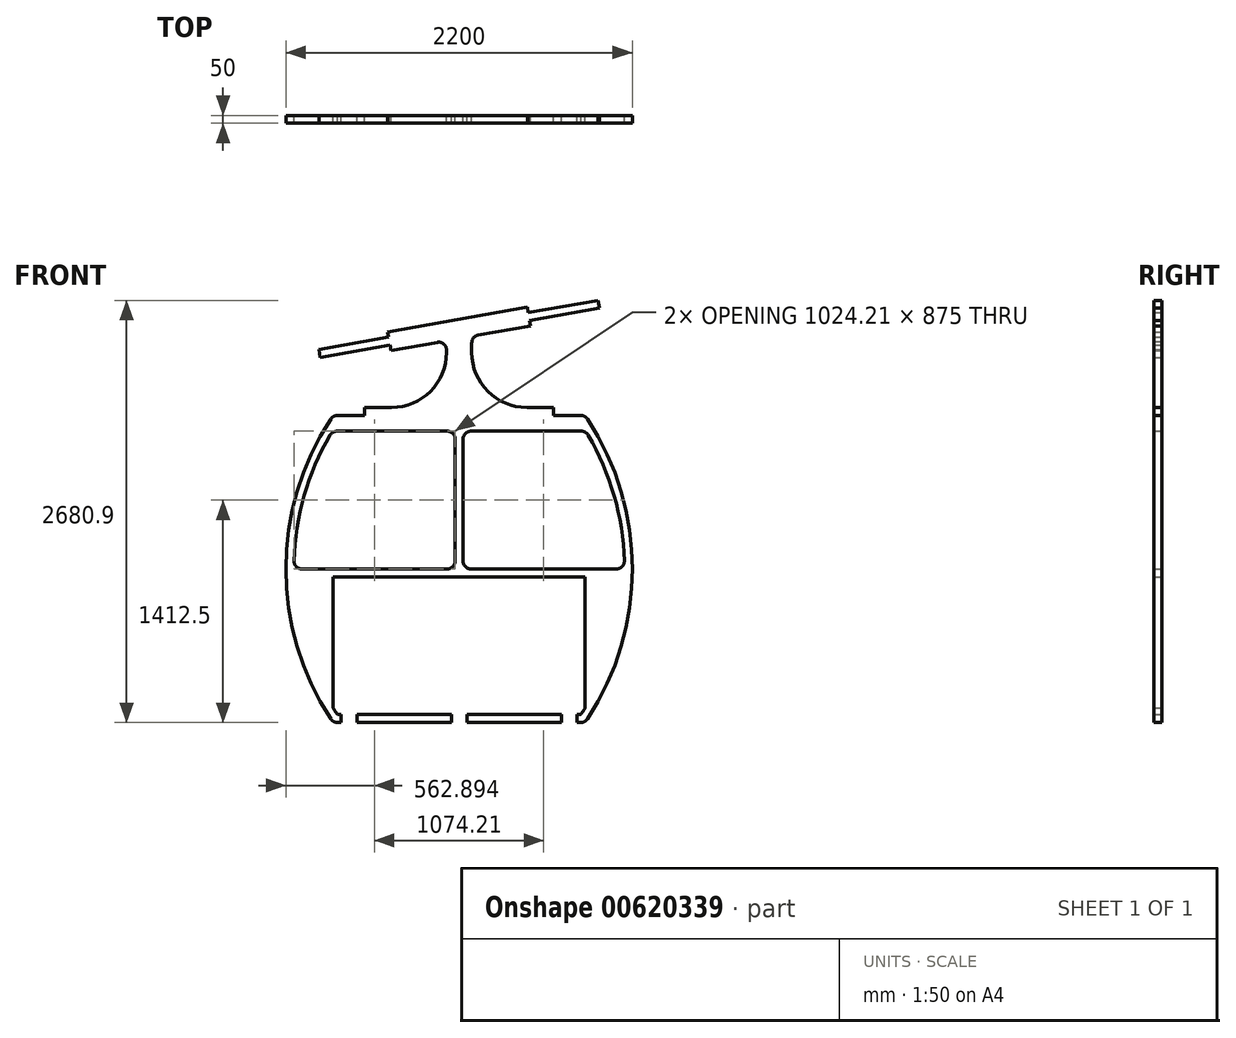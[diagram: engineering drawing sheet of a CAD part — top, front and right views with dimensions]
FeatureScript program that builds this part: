
annotation { "Feature Type Name" : "Feature", "Feature Type Description" : "" }
export const myFeature = defineFeature(function(context is Context, id is Id, definition is map)
    precondition{}
    {
        {
            var Q0;
            Q0=qCreatedBy(makeId("Front.planeOp"),FACE);
            var sketch = newSketch(context, id + "F0", { "sketchPlane" : qUnion([Q0])});
            skLineSegment(sketch, "E0.bottom", {"start": v(-1600, 1950) * mm, "end": v(0, 1950) * mm});
            skLineSegment(sketch, "E0.top", {"start": v(-1600, 0) * mm, "end": v(0, 0) * mm});
            skLineSegment(sketch, "E0.left", {"start": v(-1600, 1950) * mm, "end": v(-1600, 0) * mm});
            skLineSegment(sketch, "E0.right", {"start": v(0, 1950) * mm, "end": v(0, 0) * mm});
            skArc(sketch, "E1", {"start": v(0, 0) * mm, "mid": v(300, 975) * mm, "end": v(0, 1950) * mm});
            skArc(sketch, "E2", {"start": v(-1600, 1950) * mm, "mid": v(-1900, 975) * mm, "end": v(-1600, 0) * mm});
            skArc(sketch, "E3", {"start": v(-1604.9, 1850) * mm, "mid": v(-1849.74, 945.42) * mm, "end": v(-1573.28, 50) * mm});
            skArc(sketch, "E4", {"start": v(-26.72, 50) * mm, "mid": v(249.74, 945.42) * mm, "end": v(4.9, 1850) * mm});
            skLineSegment(sketch, "E5", {"start": v(-1850, 975) * mm, "end": v(250, 975) * mm});
            skPoint(sketch, "E5.startSnap0", {"position": v(-1900, 975) * mm});
            skLineSegment(sketch, "E6", {"start": v(-1604.9, 1850) * mm, "end": v(4.9, 1850) * mm});
            skLineSegment(sketch, "E7", {"start": v(-1573.28, 50) * mm, "end": v(-26.72, 50) * mm});
            skLineSegment(sketch, "E8", {"start": v(-800, 1950) * mm, "end": v(-800, 975) * mm});
            skLineSegment(sketch, "E9", {"start": v(-1400, 1950) * mm, "end": v(-1400, 2000) * mm});
            skLineSegment(sketch, "E10", {"start": v(-200, 1950) * mm, "end": v(-200, 2000) * mm});
            skLineSegment(sketch, "E11", {"start": v(-880, 2500) * mm, "end": v(-880, 2350) * mm});
            skLineSegment(sketch, "E12", {"start": v(-720, 2500) * mm, "end": v(-720, 2350) * mm});
            skLineSegment(sketch, "E13", {"start": v(-880, 2500) * mm, "end": v(-720, 2500) * mm});
            skLineSegment(sketch, "E14", {"start": v(-825, 1850) * mm, "end": v(-825, 975) * mm});
            skLineSegment(sketch, "E15", {"start": v(-825, 975) * mm, "end": v(-775, 975) * mm});
            skLineSegment(sketch, "E16", {"start": v(-775, 975) * mm, "end": v(-775, 1850) * mm});
            skLineSegment(sketch, "E17", {"start": v(-1400, 2000) * mm, "end": v(-1230, 2000) * mm});
            skLineSegment(sketch, "E18", {"start": v(-200, 2000) * mm, "end": v(-370, 2000) * mm});
            skArc(sketch, "E19", {"start": v(-1230, 2000) * mm, "mid": v(-982.51, 2102.51) * mm, "end": v(-880, 2350) * mm});
            skArc(sketch, "E20", {"start": v(-720, 2350) * mm, "mid": v(-617.49, 2102.51) * mm, "end": v(-370, 2000) * mm});
            skLineSegment(sketch, "E21", {"start": v(-1243.16, 2421.86) * mm, "end": v(-356.84, 2578.14) * mm});
            skCircle(sketch, "E22", {"center": v(-1243.16, 2421.86) * mm, "radius": 60 * mm});
            skCircle(sketch, "E23", {"center": v(-356.84, 2578.14) * mm, "radius": 60 * mm});
            skLineSegment(sketch, "E24", {"start": v(-810.42, 2559.09) * mm, "end": v(-800, 2500) * mm});
            skPoint(sketch, "E25.end.orphan", {"position": v(-1450.54, 2446.22) * mm});
            skPoint(sketch, "E26.start.orphan", {"position": v(-170.3, 2671.96) * mm});
            skLineSegment(sketch, "E27", {"start": v(-367.26, 2637.23) * mm, "end": v(-1253.58, 2480.95) * mm});
            skLineSegment(sketch, "E28", {"start": v(-1232.74, 2362.77) * mm, "end": v(-346.42, 2519.05) * mm});
            skLineSegment(sketch, "E29", {"start": v(81.99, 2680.9) * mm, "end": v(-1690.67, 2368.34) * mm});
            skLineSegment(sketch, "E30", {"start": v(-1690.67, 2368.34) * mm, "end": v(-1681.99, 2319.1) * mm});
            skLineSegment(sketch, "E31", {"start": v(-1681.99, 2319.1) * mm, "end": v(90.67, 2631.66) * mm});
            skLineSegment(sketch, "E32", {"start": v(90.67, 2631.66) * mm, "end": v(81.99, 2680.9) * mm});
            skLineSegment(sketch, "E33", {"start": v(-1253.58, 2480.95) * mm, "end": v(-1232.74, 2362.77) * mm});
            skLineSegment(sketch, "E34", {"start": v(-367.26, 2637.23) * mm, "end": v(-346.42, 2519.05) * mm});
            skLineSegment(sketch, "E35", {"start": v(-1899.28, 925) * mm, "end": v(299.28, 925) * mm});
            skLineSegment(sketch, "E36", {"start": v(-825, 975) * mm, "end": v(-825, 925) * mm});
            skLineSegment(sketch, "E37", {"start": v(-775, 975) * mm, "end": v(-775, 925) * mm});
            skLineSegment(sketch, "E38", {"start": v(-1550, 0) * mm, "end": v(-1550, 50) * mm});
            skLineSegment(sketch, "E39", {"start": v(-1550, 50) * mm, "end": v(-1450, 50) * mm});
            skLineSegment(sketch, "E40", {"start": v(-1450, 50) * mm, "end": v(-1450, 0) * mm});
            skLineSegment(sketch, "E41", {"start": v(-850, 0) * mm, "end": v(-850, 50) * mm});
            skLineSegment(sketch, "E42", {"start": v(-850, 50) * mm, "end": v(-750, 50) * mm});
            skLineSegment(sketch, "E43", {"start": v(-750, 50) * mm, "end": v(-750, 0) * mm});
            skLineSegment(sketch, "E44", {"start": v(-150, 0) * mm, "end": v(-150, 50) * mm});
            skLineSegment(sketch, "E45", {"start": v(-150, 50) * mm, "end": v(-50, 50) * mm});
            skLineSegment(sketch, "E46", {"start": v(-50, 50) * mm, "end": v(-50, 0) * mm});
            skLineSegment(sketch, "E47", {"start": v(-800, 50) * mm, "end": v(-800, 0) * mm});
            skSolve(sketch);
        }
        {
            var Q0;
            {var subQ0=sQuery(id+"F0.wireOp",EDGE,"E40");var subQ1=sQuery(id+"F0.wireOp",EDGE,"E0.top");var subQ2=makeQuery(id+"F0.imprint","INTERSECT",VERTEX,{"derivedFrom":[subQ1,subQ0]});Q0=makeQuery(id+"F0.imprint","IMPRINT",FACE,{"disambiguationData":[TD([[makeQuery(id+"F0.imprint","IMPRINT",EDGE,{"disambiguationData":[TD([[subQ2,-1.0]])],"derivedFrom":subQ1}),1.0]])]});}
            var Q1;
            {var subQ0=sQuery(id+"F0.wireOp",EDGE,"E43");var subQ1=sQuery(id+"F0.wireOp",EDGE,"E0.top");var subQ2=makeQuery(id+"F0.imprint","INTERSECT",VERTEX,{"derivedFrom":[subQ1,subQ0]});Q1=makeQuery(id+"F0.imprint","IMPRINT",FACE,{"disambiguationData":[TD([[makeQuery(id+"F0.imprint","IMPRINT",EDGE,{"disambiguationData":[TD([[subQ2,-1.0]])],"derivedFrom":subQ1}),1.0]])]});}
            var Q2;
            {var subQ11=sQuery(id+"F0.wireOp",EDGE,"E39");Q2=makeQuery(id+"F0.imprint","IMPRINT",FACE,{"disambiguationData":[TD([[makeQuery(id+"F0.imprint","IMPRINT",EDGE,{"derivedFrom":subQ11}),1.0]])]});}
            var Q3;
            {var subQ1=sQuery(id+"F0.wireOp",EDGE,"E0.left");var subQ3=sQuery(id+"F0.wireOp",EDGE,"E3");var subQ4=makeQuery(id+"F0.imprint","INTERSECT",VERTEX,{"derivedFrom":[subQ1,subQ3]});Q3=makeQuery(id+"F0.imprint","IMPRINT",FACE,{"disambiguationData":[TD([[makeQuery(id+"F0.imprint","IMPRINT",EDGE,{"disambiguationData":[TD([[subQ4,1.0]])],"derivedFrom":subQ3}),-1.0]])]});}
            var Q4;
            {var subQ4=sQuery(id+"F0.wireOp",EDGE,"E0.bottom");var subQ6=sQuery(id+"F0.wireOp",EDGE,"E8");var subQ7=makeQuery(id+"F0.imprint","INTERSECT",VERTEX,{"derivedFrom":[subQ4,subQ6]});Q4=makeQuery(id+"F0.imprint","IMPRINT",FACE,{"disambiguationData":[TD([[makeQuery(id+"F0.imprint","IMPRINT",EDGE,{"disambiguationData":[TD([[subQ7,1.0]])],"derivedFrom":subQ4}),-1.0]])]});}
            var Q5;
            {var subQ2=sQuery(id+"F0.wireOp",EDGE,"E8");var subQ4=sQuery(id+"F0.wireOp",EDGE,"E0.bottom");var subQ5=makeQuery(id+"F0.imprint","INTERSECT",VERTEX,{"derivedFrom":[subQ4,subQ2]});Q5=makeQuery(id+"F0.imprint","IMPRINT",FACE,{"disambiguationData":[TD([[makeQuery(id+"F0.imprint","IMPRINT",EDGE,{"disambiguationData":[TD([[subQ5,-1.0]])],"derivedFrom":subQ4}),-1.0]])]});}
            var Q6;
            {var subQ1=sQuery(id+"F0.wireOp",EDGE,"E0.right");var subQ3=sQuery(id+"F0.wireOp",EDGE,"E4");var subQ4=makeQuery(id+"F0.imprint","INTERSECT",VERTEX,{"derivedFrom":[subQ1,subQ3]});Q6=makeQuery(id+"F0.imprint","IMPRINT",FACE,{"disambiguationData":[TD([[makeQuery(id+"F0.imprint","IMPRINT",EDGE,{"disambiguationData":[TD([[subQ4,-1.0]])],"derivedFrom":subQ3}),-1.0]])]});}
            var Q7;
            {var subQ8=sQuery(id+"F0.wireOp",EDGE,"E9");Q7=makeQuery(id+"F0.imprint","IMPRINT",FACE,{"disambiguationData":[TD([[makeQuery(id+"F0.imprint","IMPRINT",EDGE,{"derivedFrom":subQ8}),-1.0]])]});}
            var Q8;
            {var subQ0=sQuery(id+"F0.wireOp",EDGE,"E14");Q8=makeQuery(id+"F0.imprint","IMPRINT",FACE,{"disambiguationData":[TD([[makeQuery(id+"F0.imprint","IMPRINT",EDGE,{"derivedFrom":subQ0}),1.0]])]});}
            var Q9;
            {var subQ0=sQuery(id+"F0.wireOp",EDGE,"E16");Q9=makeQuery(id+"F0.imprint","IMPRINT",FACE,{"disambiguationData":[TD([[makeQuery(id+"F0.imprint","IMPRINT",EDGE,{"derivedFrom":subQ0}),1.0]])]});}
            var Q10;
            {var subQ0=sQuery(id+"F0.wireOp",EDGE,"E21");var subQ1=sQuery(id+"F0.wireOp",EDGE,"E11");var subQ2=makeQuery(id+"F0.imprint","INTERSECT",VERTEX,{"derivedFrom":[subQ1,subQ0]});Q10=makeQuery(id+"F0.imprint","IMPRINT",FACE,{"disambiguationData":[TD([[makeQuery(id+"F0.imprint","IMPRINT",EDGE,{"disambiguationData":[TD([[subQ2,-1.0]])],"derivedFrom":subQ1}),-1.0]])]});}
            var Q11;
            {var subQ0=sQuery(id+"F0.wireOp",EDGE,"E33");var subQ1=sQuery(id+"F0.wireOp",EDGE,"E21");var subQ2=makeQuery(id+"F0.imprint","INTERSECT",VERTEX,{"derivedFrom":[subQ1,subQ0]});Q11=makeQuery(id+"F0.imprint","IMPRINT",FACE,{"disambiguationData":[TD([[makeQuery(id+"F0.imprint","IMPRINT",EDGE,{"disambiguationData":[TD([[subQ2,-1.0]])],"derivedFrom":subQ1}),1.0]])]});}
            var Q12;
            {var subQ1=sQuery(id+"F0.wireOp",EDGE,"E11");var subQ5=sQuery(id+"F0.wireOp",EDGE,"E13");var subQ6=makeQuery(id+"F0.imprint","INTERSECT",VERTEX,{"derivedFrom":[subQ1,subQ5]});Q12=makeQuery(id+"F0.imprint","IMPRINT",FACE,{"disambiguationData":[TD([[makeQuery(id+"F0.imprint","IMPRINT",EDGE,{"disambiguationData":[TD([[subQ6,-1.0]])],"derivedFrom":subQ1}),-1.0]])]});}
            var Q13;
            {var subQ0=sQuery(id+"F0.wireOp",EDGE,"E28");var subQ1=sQuery(id+"F0.wireOp",EDGE,"E11");var subQ2=makeQuery(id+"F0.imprint","INTERSECT",VERTEX,{"derivedFrom":[subQ1,subQ0]});Q13=makeQuery(id+"F0.imprint","IMPRINT",FACE,{"disambiguationData":[TD([[makeQuery(id+"F0.imprint","IMPRINT",EDGE,{"disambiguationData":[TD([[subQ2,1.0]])],"derivedFrom":subQ1}),-1.0]])]});}
            var Q14;
            {var subQ3=sQuery(id+"F0.wireOp",EDGE,"E21");var subQ5=sQuery(id+"F0.wireOp",EDGE,"E11");var subQ6=makeQuery(id+"F0.imprint","INTERSECT",VERTEX,{"derivedFrom":[subQ5,subQ3]});Q14=makeQuery(id+"F0.imprint","IMPRINT",FACE,{"disambiguationData":[TD([[makeQuery(id+"F0.imprint","IMPRINT",EDGE,{"disambiguationData":[TD([[subQ6,-1.0]])],"derivedFrom":subQ5}),1.0]])]});}
            var Q15;
            {var subQ0=sQuery(id+"F0.wireOp",EDGE,"E34");var subQ1=sQuery(id+"F0.wireOp",EDGE,"E21");var subQ2=makeQuery(id+"F0.imprint","INTERSECT",VERTEX,{"derivedFrom":[subQ1,subQ0]});Q15=makeQuery(id+"F0.imprint","IMPRINT",FACE,{"disambiguationData":[TD([[makeQuery(id+"F0.imprint","IMPRINT",EDGE,{"disambiguationData":[TD([[subQ2,1.0]])],"derivedFrom":subQ1}),1.0]])]});}
            var Q16;
            {var subQ5=sQuery(id+"F0.wireOp",EDGE,"E13");var subQ7=sQuery(id+"F0.wireOp",EDGE,"E12");var subQ8=makeQuery(id+"F0.imprint","INTERSECT",VERTEX,{"derivedFrom":[subQ7,subQ5]});Q16=makeQuery(id+"F0.imprint","IMPRINT",FACE,{"disambiguationData":[TD([[makeQuery(id+"F0.imprint","IMPRINT",EDGE,{"disambiguationData":[TD([[subQ8,-1.0]])],"derivedFrom":subQ7}),1.0]])]});}
            var Q17;
            {var subQ0=sQuery(id+"F0.wireOp",EDGE,"E13");var subQ1=sQuery(id+"F0.wireOp",EDGE,"E11");var subQ2=makeQuery(id+"F0.imprint","INTERSECT",VERTEX,{"derivedFrom":[subQ1,subQ0]});Q17=makeQuery(id+"F0.imprint","IMPRINT",FACE,{"disambiguationData":[TD([[makeQuery(id+"F0.imprint","IMPRINT",EDGE,{"disambiguationData":[TD([[subQ2,-1.0]])],"derivedFrom":subQ1}),1.0]])]});}
            var Q18;
            {var subQ0=sQuery(id+"F0.wireOp",EDGE,"E27");var subQ5=sQuery(id+"F0.wireOp",EDGE,"E24");var subQ6=makeQuery(id+"F0.imprint","INTERSECT",VERTEX,{"derivedFrom":[subQ5,subQ0]});Q18=makeQuery(id+"F0.imprint","IMPRINT",FACE,{"disambiguationData":[TD([[makeQuery(id+"F0.imprint","IMPRINT",EDGE,{"disambiguationData":[TD([[subQ6,-1.0]])],"derivedFrom":subQ5}),1.0]])]});}
            var Q19;
            {var subQ1=sQuery(id+"F0.wireOp",EDGE,"E21");var subQ3=sQuery(id+"F0.wireOp",EDGE,"E23");var subQ4=makeQuery(id+"F0.imprint","INTERSECT",VERTEX,{"derivedFrom":[subQ1,subQ3]});Q19=makeQuery(id+"F0.imprint","IMPRINT",FACE,{"disambiguationData":[TD([[makeQuery(id+"F0.imprint","IMPRINT",EDGE,{"disambiguationData":[TD([[subQ4,1.0]])],"derivedFrom":subQ3}),-1.0]])]});}
            var Q20;
            {var subQ0=sQuery(id+"F0.wireOp",EDGE,"E27");var subQ5=sQuery(id+"F0.wireOp",EDGE,"E24");var subQ6=makeQuery(id+"F0.imprint","INTERSECT",VERTEX,{"derivedFrom":[subQ5,subQ0]});Q20=makeQuery(id+"F0.imprint","IMPRINT",FACE,{"disambiguationData":[TD([[makeQuery(id+"F0.imprint","IMPRINT",EDGE,{"disambiguationData":[TD([[subQ6,-1.0]])],"derivedFrom":subQ5}),-1.0]])]});}
            var Q21;
            {var subQ0=sQuery(id+"F0.wireOp",EDGE,"E28");var subQ1=sQuery(id+"F0.wireOp",EDGE,"E12");var subQ2=makeQuery(id+"F0.imprint","INTERSECT",VERTEX,{"derivedFrom":[subQ1,subQ0]});Q21=makeQuery(id+"F0.imprint","IMPRINT",FACE,{"disambiguationData":[TD([[makeQuery(id+"F0.imprint","IMPRINT",EDGE,{"disambiguationData":[TD([[subQ2,1.0]])],"derivedFrom":subQ1}),1.0]])]});}
            var Q22;
            {var subQ0=sQuery(id+"F0.wireOp",EDGE,"E28");var subQ1=sQuery(id+"F0.wireOp",EDGE,"E11");var subQ2=makeQuery(id+"F0.imprint","INTERSECT",VERTEX,{"derivedFrom":[subQ1,subQ0]});Q22=makeQuery(id+"F0.imprint","IMPRINT",FACE,{"disambiguationData":[TD([[makeQuery(id+"F0.imprint","IMPRINT",EDGE,{"disambiguationData":[TD([[subQ2,1.0]])],"derivedFrom":subQ1}),1.0]])]});}
            var Q23;
            {var subQ0=sQuery(id+"F0.wireOp",EDGE,"E33");var subQ1=sQuery(id+"F0.wireOp",EDGE,"E21");var subQ2=makeQuery(id+"F0.imprint","INTERSECT",VERTEX,{"derivedFrom":[subQ1,subQ0]});Q23=makeQuery(id+"F0.imprint","IMPRINT",FACE,{"disambiguationData":[TD([[makeQuery(id+"F0.imprint","IMPRINT",EDGE,{"disambiguationData":[TD([[subQ2,-1.0]])],"derivedFrom":subQ1}),-1.0]])]});}
            var Q24;
            {var subQ0=sQuery(id+"F0.wireOp",EDGE,"E34");var subQ1=sQuery(id+"F0.wireOp",EDGE,"E21");var subQ2=makeQuery(id+"F0.imprint","INTERSECT",VERTEX,{"derivedFrom":[subQ1,subQ0]});Q24=makeQuery(id+"F0.imprint","IMPRINT",FACE,{"disambiguationData":[TD([[makeQuery(id+"F0.imprint","IMPRINT",EDGE,{"disambiguationData":[TD([[subQ2,1.0]])],"derivedFrom":subQ1}),-1.0]])]});}
            var Q25;
            {var subQ5=sQuery(id+"F0.wireOp",EDGE,"E30");Q25=makeQuery(id+"F0.imprint","IMPRINT",FACE,{"disambiguationData":[TD([[makeQuery(id+"F0.imprint","IMPRINT",EDGE,{"derivedFrom":subQ5}),1.0]])]});}
            var Q26;
            {var subQ1=sQuery(id+"F0.wireOp",EDGE,"E22");var subQ3=sQuery(id+"F0.wireOp",EDGE,"E29");var subQ4=makeQuery(id+"F0.imprint","INTERSECT",VERTEX,{"disambiguationData":[OD(1.0)],"derivedFrom":[subQ1,subQ3]});Q26=makeQuery(id+"F0.imprint","IMPRINT",FACE,{"disambiguationData":[TD([[makeQuery(id+"F0.imprint","IMPRINT",EDGE,{"disambiguationData":[TD([[subQ4,-1.0]])],"derivedFrom":subQ3}),-1.0]])]});}
            var Q27;
            {var subQ1=sQuery(id+"F0.wireOp",EDGE,"E23");var subQ3=sQuery(id+"F0.wireOp",EDGE,"E31");var subQ4=makeQuery(id+"F0.imprint","INTERSECT",VERTEX,{"disambiguationData":[OD(1.0)],"derivedFrom":[subQ1,subQ3]});Q27=makeQuery(id+"F0.imprint","IMPRINT",FACE,{"disambiguationData":[TD([[makeQuery(id+"F0.imprint","IMPRINT",EDGE,{"disambiguationData":[TD([[subQ4,-1.0]])],"derivedFrom":subQ3}),-1.0]])]});}
            var Q28;
            {var subQ5=sQuery(id+"F0.wireOp",EDGE,"E32");Q28=makeQuery(id+"F0.imprint","IMPRINT",FACE,{"disambiguationData":[TD([[makeQuery(id+"F0.imprint","IMPRINT",EDGE,{"derivedFrom":subQ5}),1.0]])]});}
            var Q29;
            {var subQ2=sQuery(id+"F0.wireOp",EDGE,"E29");var subQ5=sQuery(id+"F0.wireOp",EDGE,"E22");var subQ8=makeQuery(id+"F0.imprint","INTERSECT",VERTEX,{"disambiguationData":[OD(0.0)],"derivedFrom":[subQ5,subQ2]});Q29=makeQuery(id+"F0.imprint","IMPRINT",FACE,{"disambiguationData":[TD([[makeQuery(id+"F0.imprint","IMPRINT",EDGE,{"disambiguationData":[TD([[subQ8,-1.0]])],"derivedFrom":subQ5}),1.0]])]});}
            var Q30;
            {var subQ2=sQuery(id+"F0.wireOp",EDGE,"E29");var subQ5=sQuery(id+"F0.wireOp",EDGE,"E23");var subQ8=makeQuery(id+"F0.imprint","INTERSECT",VERTEX,{"disambiguationData":[OD(0.0)],"derivedFrom":[subQ5,subQ2]});Q30=makeQuery(id+"F0.imprint","IMPRINT",FACE,{"disambiguationData":[TD([[makeQuery(id+"F0.imprint","IMPRINT",EDGE,{"disambiguationData":[TD([[subQ8,1.0]])],"derivedFrom":subQ5}),1.0]])]});}
            var Q31;
            {var subQ1=sQuery(id+"F0.wireOp",EDGE,"E23");var subQ3=sQuery(id+"F0.wireOp",EDGE,"E29");var subQ4=makeQuery(id+"F0.imprint","INTERSECT",VERTEX,{"disambiguationData":[OD(1.0)],"derivedFrom":[subQ1,subQ3]});Q31=makeQuery(id+"F0.imprint","IMPRINT",FACE,{"disambiguationData":[TD([[makeQuery(id+"F0.imprint","IMPRINT",EDGE,{"disambiguationData":[TD([[subQ4,1.0]])],"derivedFrom":subQ3}),-1.0]])]});}
            var Q32;
            {var subQ1=sQuery(id+"F0.wireOp",EDGE,"E22");var subQ3=sQuery(id+"F0.wireOp",EDGE,"E31");var subQ4=makeQuery(id+"F0.imprint","INTERSECT",VERTEX,{"disambiguationData":[OD(1.0)],"derivedFrom":[subQ1,subQ3]});Q32=makeQuery(id+"F0.imprint","IMPRINT",FACE,{"disambiguationData":[TD([[makeQuery(id+"F0.imprint","IMPRINT",EDGE,{"disambiguationData":[TD([[subQ4,1.0]])],"derivedFrom":subQ3}),-1.0]])]});}
            var Q33;
            {var subQ0=sQuery(id+"F0.wireOp",EDGE,"E35");var subQ1=sQuery(id+"F0.wireOp",EDGE,"E0.left");var subQ2=makeQuery(id+"F0.imprint","INTERSECT",VERTEX,{"derivedFrom":[subQ1,subQ0]});Q33=makeQuery(id+"F0.imprint","IMPRINT",FACE,{"disambiguationData":[TD([[makeQuery(id+"F0.imprint","IMPRINT",EDGE,{"disambiguationData":[TD([[subQ2,-1.0]])],"derivedFrom":subQ1}),-1.0]])]});}
            var Q34;
            {var subQ0=sQuery(id+"F0.wireOp",EDGE,"E35");var subQ1=sQuery(id+"F0.wireOp",EDGE,"E0.right");var subQ2=makeQuery(id+"F0.imprint","INTERSECT",VERTEX,{"derivedFrom":[subQ1,subQ0]});Q34=makeQuery(id+"F0.imprint","IMPRINT",FACE,{"disambiguationData":[TD([[makeQuery(id+"F0.imprint","IMPRINT",EDGE,{"disambiguationData":[TD([[subQ2,-1.0]])],"derivedFrom":subQ1}),1.0]])]});}
            var Q35;
            {var subQ1=sQuery(id+"F0.wireOp",EDGE,"E4");var subQ3=makeQuery(id+"F0.imprint","INTERSECT",VERTEX,{"derivedFrom":[subQ1,sQuery(id+"F0.wireOp",EDGE,"E5")]});Q35=makeQuery(id+"F0.imprint","IMPRINT",FACE,{"disambiguationData":[TD([[makeQuery(id+"F0.imprint","IMPRINT",EDGE,{"disambiguationData":[TD([[subQ3,1.0]])],"derivedFrom":subQ1}),-1.0]])]});}
            var Q36;
            {var subQ0=sQuery(id+"F0.wireOp",EDGE,"E6");var subQ1=sQuery(id+"F0.wireOp",EDGE,"E3");var subQ2=makeQuery(id+"F0.imprint","INTERSECT",VERTEX,{"derivedFrom":[subQ1,subQ0]});Q36=makeQuery(id+"F0.imprint","IMPRINT",FACE,{"disambiguationData":[TD([[makeQuery(id+"F0.imprint","IMPRINT",EDGE,{"disambiguationData":[TD([[subQ2,-1.0]])],"derivedFrom":subQ1}),-1.0]])]});}
            var Q37;
            {var subQ0=sQuery(id+"F0.wireOp",EDGE,"E36");Q37=makeQuery(id+"F0.imprint","IMPRINT",FACE,{"disambiguationData":[TD([[makeQuery(id+"F0.imprint","IMPRINT",EDGE,{"derivedFrom":subQ0}),1.0]])]});}
            var Q38;
            {var subQ0=sQuery(id+"F0.wireOp",EDGE,"E7");var subQ1=sQuery(id+"F0.wireOp",EDGE,"E4");var subQ2=makeQuery(id+"F0.imprint","INTERSECT",VERTEX,{"derivedFrom":[subQ1,subQ0]});Q38=makeQuery(id+"F0.imprint","IMPRINT",FACE,{"disambiguationData":[TD([[makeQuery(id+"F0.imprint","IMPRINT",EDGE,{"disambiguationData":[TD([[subQ2,-1.0]])],"derivedFrom":subQ1}),-1.0]])]});}
            var Q39;
            {var subQ3=sQuery(id+"F0.wireOp",EDGE,"E3");var subQ5=sQuery(id+"F0.wireOp",EDGE,"E7");var subQ6=makeQuery(id+"F0.imprint","INTERSECT",VERTEX,{"derivedFrom":[subQ3,subQ5]});Q39=makeQuery(id+"F0.imprint","IMPRINT",FACE,{"disambiguationData":[TD([[makeQuery(id+"F0.imprint","IMPRINT",EDGE,{"disambiguationData":[TD([[subQ6,1.0]])],"derivedFrom":subQ3}),-1.0]])]});}
            var Q40;
            {var subQ5=sQuery(id+"F0.wireOp",EDGE,"E36");Q40=makeQuery(id+"F0.imprint","IMPRINT",FACE,{"disambiguationData":[TD([[makeQuery(id+"F0.imprint","IMPRINT",EDGE,{"derivedFrom":subQ5}),-1.0]])]});}
            var Q41;
            {var subQ5=sQuery(id+"F0.wireOp",EDGE,"E37");Q41=makeQuery(id+"F0.imprint","IMPRINT",FACE,{"disambiguationData":[TD([[makeQuery(id+"F0.imprint","IMPRINT",EDGE,{"derivedFrom":subQ5}),1.0]])]});}
            var Q42;
            {var subQ0=sQuery(id+"F0.wireOp",EDGE,"E5");var subQ1=sQuery(id+"F0.wireOp",EDGE,"E0.left");var subQ2=makeQuery(id+"F0.imprint","INTERSECT",VERTEX,{"derivedFrom":[subQ1,subQ0]});Q42=makeQuery(id+"F0.imprint","IMPRINT",FACE,{"disambiguationData":[TD([[makeQuery(id+"F0.imprint","IMPRINT",EDGE,{"disambiguationData":[TD([[subQ2,-1.0]])],"derivedFrom":subQ1}),-1.0]])]});}
            var Q43;
            {var subQ0=sQuery(id+"F0.wireOp",EDGE,"E5");var subQ1=sQuery(id+"F0.wireOp",EDGE,"E0.right");var subQ2=makeQuery(id+"F0.imprint","INTERSECT",VERTEX,{"derivedFrom":[subQ1,subQ0]});Q43=makeQuery(id+"F0.imprint","IMPRINT",FACE,{"disambiguationData":[TD([[makeQuery(id+"F0.imprint","IMPRINT",EDGE,{"disambiguationData":[TD([[subQ2,-1.0]])],"derivedFrom":subQ1}),1.0]])]});}
            var Q44;
            {var subQ0=sQuery(id+"F0.wireOp",EDGE,"E3");var subQ1=makeQuery(id+"F0.imprint","INTERSECT",VERTEX,{"derivedFrom":[subQ0,sQuery(id+"F0.wireOp",EDGE,"E5")]});Q44=makeQuery(id+"F0.imprint","IMPRINT",FACE,{"disambiguationData":[TD([[makeQuery(id+"F0.imprint","IMPRINT",EDGE,{"disambiguationData":[TD([[subQ1,1.0]])],"derivedFrom":subQ0}),-1.0]])]});}
            extrude(context, id + "F1", {"entities" : qUnion([Q0, Q1, Q2, Q3, Q4, Q5, Q6, Q7, Q8, Q9, Q10, Q11, Q12, Q13, Q14, Q15, Q16, Q17, Q18, Q19, Q20, Q21, Q22, Q23, Q24, Q25, Q26, Q27, Q28, Q29, Q30, Q31, Q32, Q33, Q34, Q35, Q36, Q37, Q38, Q39, Q40, Q41, Q42, Q43, Q44]), "depth" : 50 * mm, "offsetDistance" : 25.4 * mm});
        }
        {
            var Q0;
            Q0=makeQuery(id+"F1.opExtrude","SWEPT_EDGE",EDGE,{"disambiguationData":[OSD([sQuery(id+"F0.wireOp",EDGE,"E3"),sQuery(id+"F0.wireOp",EDGE,"E6")])]});
            var Q1;
            Q1=makeQuery(id+"F1.opExtrude","SWEPT_EDGE",EDGE,{"disambiguationData":[OSD([sQuery(id+"F0.wireOp",EDGE,"E6"),sQuery(id+"F0.wireOp",EDGE,"E14")])]});
            var Q2;
            Q2=makeQuery(id+"F1.opExtrude","SWEPT_EDGE",EDGE,{"disambiguationData":[OSD([sQuery(id+"F0.wireOp",EDGE,"E3"),sQuery(id+"F0.wireOp",EDGE,"E5")])]});
            var Q3;
            Q3=makeQuery(id+"F1.opExtrude","SWEPT_EDGE",EDGE,{"disambiguationData":[OSD([sQuery(id+"F0.wireOp",EDGE,"E5"),sQuery(id+"F0.wireOp",EDGE,"E14"),sQuery(id+"F0.wireOp",EDGE,"E15"),sQuery(id+"F0.wireOp",EDGE,"E36")])]});
            var Q4;
            Q4=makeQuery(id+"F1.opExtrude","SWEPT_EDGE",EDGE,{"disambiguationData":[OSD([sQuery(id+"F0.wireOp",EDGE,"E6"),sQuery(id+"F0.wireOp",EDGE,"E16")])]});
            var Q5;
            Q5=makeQuery(id+"F1.opExtrude","SWEPT_EDGE",EDGE,{"disambiguationData":[OSD([sQuery(id+"F0.wireOp",EDGE,"E5"),sQuery(id+"F0.wireOp",EDGE,"E15"),sQuery(id+"F0.wireOp",EDGE,"E16"),sQuery(id+"F0.wireOp",EDGE,"E37")])]});
            var Q6;
            Q6=makeQuery(id+"F1.opExtrude","SWEPT_EDGE",EDGE,{"disambiguationData":[OSD([sQuery(id+"F0.wireOp",EDGE,"E4"),sQuery(id+"F0.wireOp",EDGE,"E5")])]});
            var Q7;
            Q7=makeQuery(id+"F1.opExtrude","SWEPT_EDGE",EDGE,{"disambiguationData":[OSD([sQuery(id+"F0.wireOp",EDGE,"E4"),sQuery(id+"F0.wireOp",EDGE,"E6")])]});
            var Q8;
            Q8=makeQuery(id+"F1.opExtrude","SWEPT_EDGE",EDGE,{"disambiguationData":[OSD([sQuery(id+"F0.wireOp",EDGE,"E0.bottom"),sQuery(id+"F0.wireOp",EDGE,"E0.right"),sQuery(id+"F0.wireOp",EDGE,"E1")])]});
            var Q9;
            Q9=makeQuery(id+"F1.opExtrude","SWEPT_EDGE",EDGE,{"disambiguationData":[OSD([sQuery(id+"F0.wireOp",EDGE,"E0.bottom"),sQuery(id+"F0.wireOp",EDGE,"E0.left"),sQuery(id+"F0.wireOp",EDGE,"E2")])]});
            var Q10;
            Q10=makeQuery(id+"F1.opExtrude","SWEPT_EDGE",EDGE,{"disambiguationData":[OSD([sQuery(id+"F0.wireOp",EDGE,"E0.top"),sQuery(id+"F0.wireOp",EDGE,"E0.left"),sQuery(id+"F0.wireOp",EDGE,"E2")])]});
            var Q11;
            Q11=makeQuery(id+"F1.opExtrude","SWEPT_EDGE",EDGE,{"disambiguationData":[OSD([sQuery(id+"F0.wireOp",EDGE,"E0.top"),sQuery(id+"F0.wireOp",EDGE,"E0.right"),sQuery(id+"F0.wireOp",EDGE,"E1")])]});
            var Q12;
            Q12=makeQuery(id+"F1.opExtrude","SWEPT_EDGE",EDGE,{"disambiguationData":[OSD([sQuery(id+"F0.wireOp",EDGE,"E11"),sQuery(id+"F0.wireOp",EDGE,"E28")])]});
            var Q13;
            Q13=makeQuery(id+"F1.opExtrude","SWEPT_EDGE",EDGE,{"disambiguationData":[OSD([sQuery(id+"F0.wireOp",EDGE,"E12"),sQuery(id+"F0.wireOp",EDGE,"E28")])]});
            fillet(context, id + "F2", {"entities" : qUnion([Q0, Q1, Q2, Q3, Q4, Q5, Q6, Q7, Q8, Q9, Q10, Q11, Q12, Q13]), "radius" : 50 * mm, "tangentPropagation" : true, "allowEdgeOverflow" : false});
        }
    });
